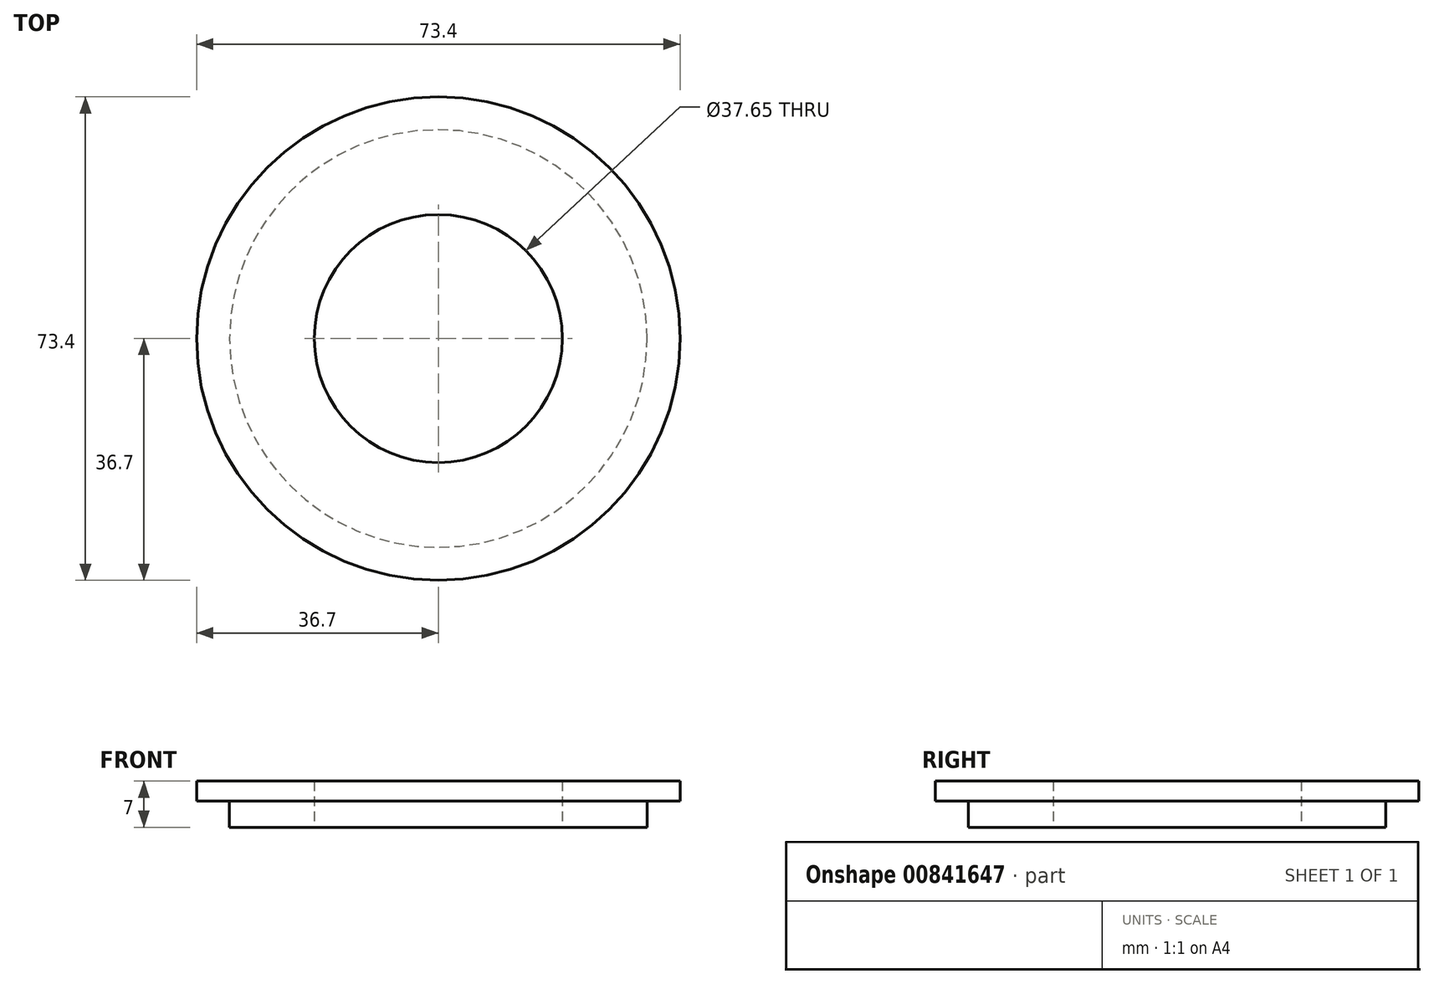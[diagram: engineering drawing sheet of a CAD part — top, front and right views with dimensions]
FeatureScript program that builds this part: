
annotation { "Feature Type Name" : "Feature", "Feature Type Description" : "" }
export const myFeature = defineFeature(function(context is Context, id is Id, definition is map)
    precondition{}
    {
        {
            var Q0;
            Q0=qCreatedBy(makeId("Top.planeOp"),FACE);
            var sketch = newSketch(context, id + "F0", { "sketchPlane" : qUnion([Q0])});
            skCircle(sketch, "E0", {"center": v(0, 0) * mm, "radius": 19.12 * mm, "construction": true});
            skCircle(sketch, "E1", {"center": v(0, 0) * mm, "radius": 32 * mm, "construction": true});
            skCircle(sketch, "E2.0", {"center": v(0, 0) * mm, "radius": 18.82 * mm});
            skCircle(sketch, "E3.0", {"center": v(0, 0) * mm, "radius": 31.7 * mm});
            skCircle(sketch, "E4.0", {"center": v(0, 0) * mm, "radius": 36.7 * mm});
            skLineSegment(sketch, "E5", {"start": v(0, 0) * mm, "end": v(0, -36.7) * mm});
            skLineSegment(sketch, "E6", {"start": v(0, 0) * mm, "end": v(-30.06, 21.05) * mm});
            skSolve(sketch);
        }
        {
            var Q0;
            {var subQ0=sQuery(id+"F0.wireOp",EDGE,"E5");var subQ1=sQuery(id+"F0.wireOp",EDGE,"E3.0");var subQ2=makeQuery(id+"F0.imprint","INTERSECT",VERTEX,{"derivedFrom":[subQ1,subQ0]});Q0=makeQuery(id+"F0.imprint","IMPRINT",FACE,{"disambiguationData":[TD([[makeQuery(id+"F0.imprint","IMPRINT",EDGE,{"disambiguationData":[TD([[subQ2,-1.0]])],"derivedFrom":subQ1}),-1.0]])]});}
            var Q1;
            {var subQ0=sQuery(id+"F0.wireOp",EDGE,"E5");var subQ1=sQuery(id+"F0.wireOp",EDGE,"E2.0");var subQ2=makeQuery(id+"F0.imprint","INTERSECT",VERTEX,{"derivedFrom":[subQ1,subQ0]});Q1=makeQuery(id+"F0.imprint","IMPRINT",FACE,{"disambiguationData":[TD([[makeQuery(id+"F0.imprint","IMPRINT",EDGE,{"disambiguationData":[TD([[subQ2,-1.0]])],"derivedFrom":subQ1}),-1.0]])]});}
            extrude(context, id + "F1", {"entities" : qUnion([Q0, Q1]), "depth" : 3 * mm, "offsetDistance" : 25 * mm});
        }
        {
            var Q0;
            {var subQ0=sQuery(id+"F0.wireOp",EDGE,"E5");var subQ1=sQuery(id+"F0.wireOp",EDGE,"E2.0");var subQ2=makeQuery(id+"F0.imprint","INTERSECT",VERTEX,{"derivedFrom":[subQ1,subQ0]});Q0=makeQuery(id+"F0.imprint","IMPRINT",FACE,{"disambiguationData":[TD([[makeQuery(id+"F0.imprint","IMPRINT",EDGE,{"disambiguationData":[TD([[subQ2,-1.0]])],"derivedFrom":subQ1}),-1.0]])]});}
            extrude(context, id + "F2", {"entities" : qUnion([Q0]), "operationType" : NewBodyOperationType.ADD, "oppositeDirection" : true, "depth" : 4 * mm, "offsetDistance" : 25 * mm});
        }
        {
            var Q0;
            {var subQ0=sQuery(id+"F0.wireOp",EDGE,"E5");var subQ1=sQuery(id+"F0.wireOp",EDGE,"E2.0");var subQ2=makeQuery(id+"F0.imprint","INTERSECT",VERTEX,{"derivedFrom":[subQ1,subQ0]});Q0=makeQuery(id+"F0.imprint","IMPRINT",FACE,{"disambiguationData":[TD([[makeQuery(id+"F0.imprint","IMPRINT",EDGE,{"disambiguationData":[TD([[subQ2,1.0]])],"derivedFrom":subQ1}),-1.0]])]});}
            var Q1;
            {var subQ0=sQuery(id+"F0.wireOp",EDGE,"E5");var subQ1=sQuery(id+"F0.wireOp",EDGE,"E3.0");var subQ2=makeQuery(id+"F0.imprint","INTERSECT",VERTEX,{"derivedFrom":[subQ1,subQ0]});Q1=makeQuery(id+"F0.imprint","IMPRINT",FACE,{"disambiguationData":[TD([[makeQuery(id+"F0.imprint","IMPRINT",EDGE,{"disambiguationData":[TD([[subQ2,1.0]])],"derivedFrom":subQ1}),-1.0]])]});}
            extrude(context, id + "F3", {"entities" : qUnion([Q0, Q1]), "depth" : 3 * mm, "offsetDistance" : 25 * mm});
        }
        {
            var Q0;
            {var subQ0=sQuery(id+"F0.wireOp",EDGE,"E5");var subQ1=sQuery(id+"F0.wireOp",EDGE,"E2.0");var subQ2=makeQuery(id+"F0.imprint","INTERSECT",VERTEX,{"derivedFrom":[subQ1,subQ0]});Q0=makeQuery(id+"F0.imprint","IMPRINT",FACE,{"disambiguationData":[TD([[makeQuery(id+"F0.imprint","IMPRINT",EDGE,{"disambiguationData":[TD([[subQ2,1.0]])],"derivedFrom":subQ1}),-1.0]])]});}
            extrude(context, id + "F4", {"entities" : qUnion([Q0]), "operationType" : NewBodyOperationType.ADD, "oppositeDirection" : true, "depth" : 4 * mm, "offsetDistance" : 25 * mm});
        }
    });
